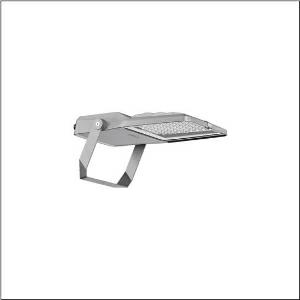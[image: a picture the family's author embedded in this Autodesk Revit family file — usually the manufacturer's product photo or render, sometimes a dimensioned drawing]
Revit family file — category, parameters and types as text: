
# Revit family: floodlight_fl_21_iq_mini___pl33t_5xa7772c5f1a_3dad
name_source: partatom
category: Lighting Fixtures
units: mm (PartAtom-declared; Revit-internal decimal feet)

## family parameters
Cut with Voids When Loaded = No
Host = Face
Light Source = No
Part Type = Normal
Room Calculation Point = No
Round Connector Dimension = Use Diameter
Shared = No

## types (1)
- --- (1 x LED, 11260 lm, 87.2 W, 4000K)
    Apparent Load = 87 VA
    CIE Flux Codes = 26 75 99 100 100
    Color Rendering = 80
    Color Temperature = 4000K
    Default Elevation = 1800 mm
    Description = Floodlight FL 21 iQ mini, floodlight, primary light control with lens, of PMMA, primary optical cover: protective disc, of toughened safety glass, transparent, light distribution: PL33T, light emission: direct distribution, installation type: surface-mounted, lamps: LED, High Power LED, rated values: 11.260lm | 87,2W | 129,1lm/W (begin service life); end service life: 11.260lm | 92,1W; at 50% lumin. flux: 5.630lm | 40,1W | 140,4lm/W, colour temperature: 4000K, colour rendering: CRI > 80, light colour: 840, light setting 1 begin service life: 100% | 11.260lm | 87,2W | 129,1lm/W | 4.000K, light setting 1 end service life: 92,1W, further light settings possible, control: Street-Remote, Auto-Match, Temp-Guard, Night-Set, Smart-Wire, Desk-Remote (wireless, voltage-free reading and setting of iQ features in the workshop via application-optimized NFC function/RFID function), optimised constant luminous flux control (CLO 2.0), pre-setting: linear dimming characteristic, with terminal, 6-pole, mains connection: 220..240V, AC, 50/60Hz, luminaire housing, of diecast aluminium, powder-coated, SITECO metallic grey (DB 702S), corrosivity category C5 mid according to DIN EN ISO 12944suitable for swimming poolschlorine-resistant, sealing non-destructively replaceable, mounting bracket, of steel, galvanised, powder-coated, SITECO metallic grey (DB 702S), protection rating (complete): IP66, insulation class (complete): insulation class II (safety insulation), certification: CE, ENEC, VDE, protection symbol: D, impact resistance: IK08, permissible operating ambient temperature: -40..+40°C, permissible operating ambient temperature for outdoor applications: -40..+50°C, standard: DIN EN 12944, LABS conformity tested according to VDMA 24364:2018-05, packaging unit: 1 piece

Light Distribution: PL33T
    Height = 70 mm
    Lamp = 1 x LED
    Lamp Light Flux = 11260 lm
    Lamp Power = 87.2 W
    Lamp count = 1
    Length = 485 mm
    Luminous efficacy = 129 lm/W
    Manufacturer = Siteco
    ModVariant = No
    Model = 5XA7772C5F1A
    Number of Poles = 1
    OnlyDefault = Yes
    Power Factor = 1
    Product Name = Floodlight FL 21 iQ mini | PL33T
    Product group = floodlight | pylon annexe
    ProductGroupID = 6201
    Protection Class = Protection class II
    Protection Degree = IP 66
    RLX_Detail_Level = 1
    RLX_Emergency_Light_Flux = 0 lm
    RLX_Emergency_Type = 0
    RLX_Emergency_Type_DB = No
    RlxData = <blob elided: 96549 chars, md5=709940b3>
    Socket = socket
    Standby Power = 0 W
    System Light Flux = 11260 lm
    System Power = 87 W
    Type Comments = factory setting: luminous flux: 100 % | dim-lin: 254 | 456 mA
    Type Image = l_1006845.jpg
    URL = http://relux.com
    VarID = @adj_148807
    Voltage = 0 V
    Weight = 0.00 kg
    Width = 337 mm

## geometry (parser evidence)
native form markers: Blend x4, Sweep x12
no freeform markers — native parametric forms only
